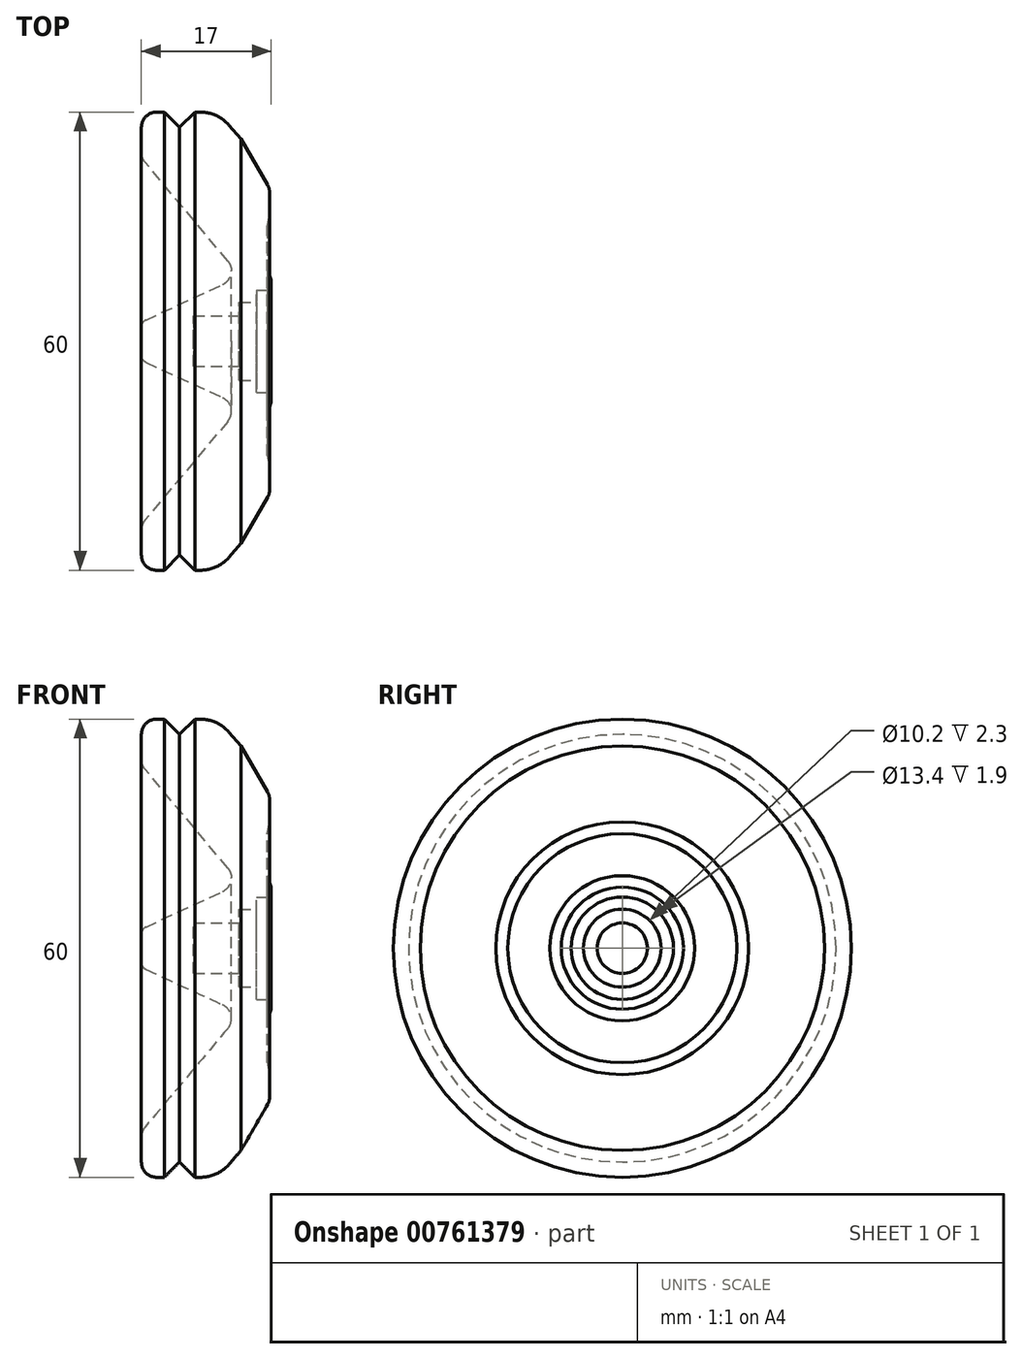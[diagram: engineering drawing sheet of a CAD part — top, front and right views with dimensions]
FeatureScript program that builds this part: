
annotation { "Feature Type Name" : "Feature", "Feature Type Description" : "" }
export const myFeature = defineFeature(function(context is Context, id is Id, definition is map)
    precondition{}
    {
        {
            var Q0;
            Q0=qCreatedBy(makeId("Front.planeOp"),FACE);
            var sketch = newSketch(context, id + "F0", { "sketchPlane" : qUnion([Q0])});
            skLineSegment(sketch, "E0", {"start": v(2, 30) * mm, "end": v(3, 30) * mm});
            skLineSegment(sketch, "E1", {"start": v(3, 30) * mm, "end": v(5, 28) * mm});
            skLineSegment(sketch, "E2", {"start": v(5, 28) * mm, "end": v(7, 30) * mm});
            skLineSegment(sketch, "E3", {"start": v(15.1, 5.1) * mm, "end": v(12.8, 5.1) * mm});
            skLineSegment(sketch, "E4", {"start": v(12.8, 5.1) * mm, "end": v(12.8, 3.3) * mm});
            skLineSegment(sketch, "E5", {"start": v(12.8, 3.3) * mm, "end": v(6.8, 3.3) * mm});
            skLineSegment(sketch, "E6", {"start": v(6.8, 3.3) * mm, "end": v(6.8, 0) * mm});
            skLineSegment(sketch, "E7", {"start": v(6.8, 0) * mm, "end": v(0, 0) * mm});
            skPoint(sketch, "E8.visualSharp", {"position": v(0, 30) * mm});
            skLineSegment(sketch, "E9", {"start": v(15.1, 5.1) * mm, "end": v(15.1, 6.7) * mm});
            skLineSegment(sketch, "E10", {"start": v(15.1, 6.7) * mm, "end": v(17, 6.7) * mm});
            skLineSegment(sketch, "E11", {"start": v(17, 6.7) * mm, "end": v(17, 8) * mm});
            skLineSegment(sketch, "E12", {"start": v(16.5, 15) * mm, "end": v(16.5, 9.5) * mm});
            skLineSegment(sketch, "E13", {"start": v(16.5, 9.5) * mm, "end": v(17, 8) * mm});
            skLineSegment(sketch, "E14", {"start": v(0, 1.86) * mm, "end": v(0, 0) * mm});
            skLineSegment(sketch, "E15", {"start": v(16.8, 16.55) * mm, "end": v(16.5, 15) * mm});
            skPoint(sketch, "E16.visualSharp", {"position": v(16.8, 20) * mm});
            skPoint(sketch, "E17.visualSharp", {"position": v(0, 24) * mm});
            skLineSegment(sketch, "E18", {"start": v(7, 30) * mm, "end": v(7.72, 30) * mm});
            skLineSegment(sketch, "E19", {"start": v(11.5, 28.28) * mm, "end": v(13.06, 26.48) * mm});
            skLineSegment(sketch, "E20", {"start": v(13.06, 26.48) * mm, "end": v(16.53, 20.46) * mm});
            skLineSegment(sketch, "E21", {"start": v(16.8, 16.55) * mm, "end": v(16.8, 19.46) * mm});
            skPoint(sketch, "E22.visualSharp", {"position": v(10, 30) * mm});
            skArc(sketch, "E22.filletArc", {"start": v(11.5, 28.28) * mm, "mid": v(9.8, 29.55) * mm, "end": v(7.72, 30) * mm});
            skArc(sketch, "E23.filletArc", {"start": v(16.8, 19.46) * mm, "mid": v(16.73, 19.98) * mm, "end": v(16.53, 20.46) * mm});
            skLineSegment(sketch, "E24", {"start": v(0, 28) * mm, "end": v(0, 24.73) * mm});
            skPoint(sketch, "E25.visualSharp", {"position": v(0, 2.5) * mm});
            skPoint(sketch, "E26.visualSharp", {"position": v(13, 8.5) * mm});
            skLineSegment(sketch, "E27", {"start": v(11.32, 10.5) * mm, "end": v(0.47, 23.44) * mm});
            skLineSegment(sketch, "E28", {"start": v(0.58, 2.77) * mm, "end": v(10.62, 7.4) * mm});
            skArc(sketch, "E29.filletArc", {"start": v(0, 24.73) * mm, "mid": v(0.12, 24.04) * mm, "end": v(0.47, 23.44) * mm});
            skArc(sketch, "E30.filletArc", {"start": v(2, 30) * mm, "mid": v(0.59, 29.41) * mm, "end": v(0, 28) * mm});
            skArc(sketch, "E31.filletArc", {"start": v(10.62, 7.4) * mm, "mid": v(11.74, 8.78) * mm, "end": v(11.32, 10.5) * mm});
            skArc(sketch, "E32.filletArc", {"start": v(0.58, 2.77) * mm, "mid": v(0.16, 2.4) * mm, "end": v(0, 1.86) * mm});
            skSolve(sketch);
        }
        {
            var Q0;
            Q0=makeQuery(id+"F0.imprint","IMPRINT",FACE,{"disambiguationData":[TD([[makeQuery(id+"F0.imprint","IMPRINT",EDGE,{"derivedFrom":sQuery(id+"F0.wireOp",EDGE,"E0")}),-1.0]])]});
            var Q1;
            Q1=sQuery(id+"F0.wireOp",EDGE,"E7");
            revolve(context, id + "F1", {"surfaceOperationType" : NewSurfaceOperationType.NEW, "entities" : qUnion([Q0]), "axis" : qUnion([Q1]), "revolveType" : RevolveType.FULL});
        }
    });
